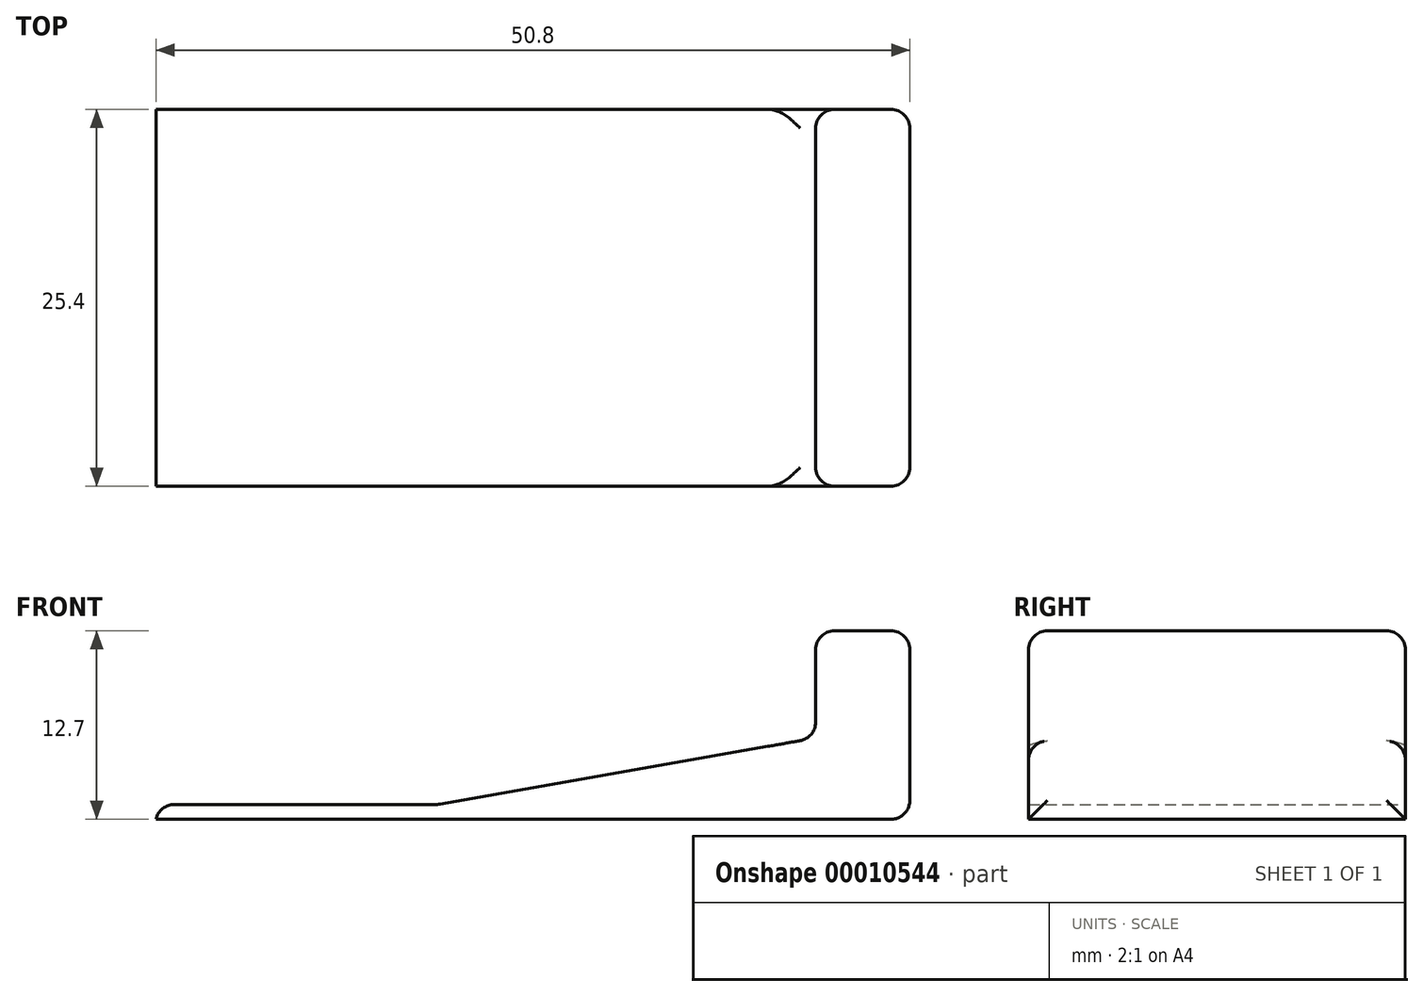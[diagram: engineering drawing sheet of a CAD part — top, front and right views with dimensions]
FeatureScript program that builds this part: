
annotation { "Feature Type Name" : "Feature", "Feature Type Description" : "" }
export const myFeature = defineFeature(function(context is Context, id is Id, definition is map)
    precondition{}
    {
        {
            var Q0;
            Q0=qCreatedBy(makeId("Front.planeOp"),FACE);
            var sketch = newSketch(context, id + "F0", { "sketchPlane" : qUnion([Q0])});
            skLineSegment(sketch, "E0", {"start": v(0, 12.7) * mm, "end": v(0, 0) * mm});
            skLineSegment(sketch, "E1", {"start": v(0, 0) * mm, "end": v(-50.8, 0) * mm});
            skLineSegment(sketch, "E2", {"start": v(-50.8, 0) * mm, "end": v(-50.8, 1) * mm});
            skLineSegment(sketch, "E3", {"start": v(-50.8, 1) * mm, "end": v(-31.75, 1) * mm});
            skLineSegment(sketch, "E4", {"start": v(-6.35, 5.48) * mm, "end": v(-6.35, 12.7) * mm});
            skLineSegment(sketch, "E5", {"start": v(-6.35, 12.7) * mm, "end": v(0, 12.7) * mm});
            skLineSegment(sketch, "E6", {"start": v(-6.35, 5.48) * mm, "end": v(-31.75, 1) * mm});
            skSolve(sketch);
        }
        {
            var Q0;
            Q0=makeQuery(id+"F0.imprint","IMPRINT",FACE,{"disambiguationData":[TD([[makeQuery(id+"F0.imprint","IMPRINT",EDGE,{"derivedFrom":sQuery(id+"F0.wireOp",EDGE,"E0")}),-1.0]])]});
            extrude(context, id + "F1", {"entities" : qUnion([Q0]), "depth" : 25.4 * mm, "symmetric" : true});
        }
        {
            var Q0;
            Q0=makeQuery(id+"F1.opExtrude","SWEPT_FACE",FACE,{"disambiguationData":[OSD([sQuery(id+"F0.wireOp",EDGE,"E4")])]});
            var Q1;
            Q1=makeQuery(id+"F1.opExtrude","SWEPT_FACE",FACE,{"disambiguationData":[OSD([sQuery(id+"F0.wireOp",EDGE,"E5")])]});
            var Q2;
            Q2=makeQuery(id+"F1.opExtrude","SWEPT_FACE",FACE,{"disambiguationData":[OSD([sQuery(id+"F0.wireOp",EDGE,"E0")])]});
            var Q3;
            Q3=makeQuery(id+"F1.opExtrude","SWEPT_EDGE",EDGE,{"disambiguationData":[OSD([sQuery(id+"F0.wireOp",EDGE,"E3"),sQuery(id+"F0.wireOp",EDGE,"E6")])]});
            var Q4;
            Q4=makeQuery(id+"F1.opExtrude","SWEPT_EDGE",EDGE,{"disambiguationData":[OSD([sQuery(id+"F0.wireOp",EDGE,"E2"),sQuery(id+"F0.wireOp",EDGE,"E3")])]});
            fillet(context, id + "F2", {"entities" : qUnion([Q0, Q1, Q2, Q3, Q4]), "radius" : 1.27 * mm, "allowEdgeOverflow" : false});
        }
    });
